# Revit family: a_reynaers_cs-59-functional_door_inside-opening-brush_doublerfa
name_source: partatom
category: Windows
revit_build: Autodesk Revit 2017 (Build: 20160225_1515(x64)
units: mm (PartAtom-declared; Revit-internal decimal feet)

## family parameters
Always vertical = Yes
Cut with Voids When Loaded = No
Host = Wall
OmniClass Number = 23.30.20.00
OmniClass Title = Windows
Room Calculation Point = No
Shared = No

## types (1)
- Frame 67mm
    Analytic Construction = <None>
    BE = No
    Date of publishing = 2015-11-19
    Default Sill Height = 0 mm  [stored 0 ft]
    Design country = Belgium
    Edition number = 1
    IFC Classification = Door
    Manufacturer = Reynaers
    Manufacturer country = Belgium
    Manufacturer name = Reynaers
    Material main = Aluminium
    Material secondary = Aluminium
    NBS Reference Code = 10-50-25-25
    NBS Reference Description = Doors, Windows And Glazing Survey Systems
    NL = Yes
    Nominal height = 0
    Nominal width = 0
    Product Guid = 852ccc50-b7c0-491e-9302-473c1b46b10f
    Product SKU = Reynaers_door_Concept_system_59
    Product data url = http://file-system.ru
    Product family = Windows & Doors
    Product group = Windows Aluminium
    QR code = http://file-system.ru
    REY Block Frame = No
    REY Brush Profile Height = 26 mm
    REY Built-In Depth = 50 mm  [stored 0.164042 ft]
    REY Butt Strip Width = 25 mm  [stored 0.082021 ft]
    REY Design = 0 mm  [stored 0 ft]
    REY Fixation Bottom = 33 mm  [stored 0.108268 ft]
    REY Frame Position MID = 82 mm  [stored 0.269029 ft]
    REY Frame Width = 67 mm
    REY Gap Floor = 13 mm
    REY Gap Width = 5 mm  [stored 0.0164042 ft]
    REY Joint Bottom = 0 mm  [stored 0 ft]
    REY Joint Width = 8 mm  [stored 0.0262467 ft]
    REY Joint Width A = 8 mm  [stored 0.0262467 ft]
    REY Joint Width B = 0 mm  [stored 0 ft]
    REY Offset Wall Ext Int = 25 mm  [stored 0.082021 ft]
    REY Offset Wall Ext Int A = 25 mm  [stored 0.082021 ft]
    REY Offset Wall Ext Int B = 0 mm  [stored 0 ft]
    REY Panel Coverage = 19 mm  [stored 0.062336 ft]
    REY Profile Rebate = 25 mm  [stored 0.082021 ft]
    REY Rebate = 30 mm  [stored 0.0984252 ft]
    REY Rebate A = 30 mm  [stored 0.0984252 ft]
    REY Rebate B = 0 mm  [stored 0 ft]
    REY Rebate TOP A = 30 mm  [stored 0.0984252 ft]
    REY Rebate TOP B = 0 mm  [stored 0 ft]
    REY Shutter = No
    REY Shutter Depth = 0 mm  [stored 0 ft]
    REY Shutter Height = 0 mm  [stored 0 ft]
    REY Shutter Position = 25 mm  [stored 0.082021 ft]
    REY Shutter Roll Height = 200 mm  [stored 0.656168 ft]
    REY Shutter Roll Material = <By Category>
    REY Sill H = 0 mm  [stored 0 ft]
    REY Sill Height = 0 mm  [stored 0 ft]
    REY Vent & Gap & 20 = 102 mm
    REY Vent Width = 77 mm  [stored 0.252625 ft]
    REY Website = www.reynaers.com
    UNSPSC Code = 301715
    URL = http://www.reynaers.com
    Uniclass 1.4 Code = JL20
    Uniclass 1.4 Description = Doors
    Uniclass 2.0 Code = SS-10-50-25-25
    Uniclass 2.0 Description = Doors, Windows And Glazing Survey Systems
    Wall Closure = By host
    Wall Exterior Width = 90 mm  [stored 0.295276 ft]
    Weight Net (Kg) = 0

note: [stored X ft] marks values corroborated as IEEE doubles in the binary element streams (Revit-internal decimal feet)

## geometry (parser evidence)
native form markers: Sweep x7
no freeform markers — native parametric forms only
